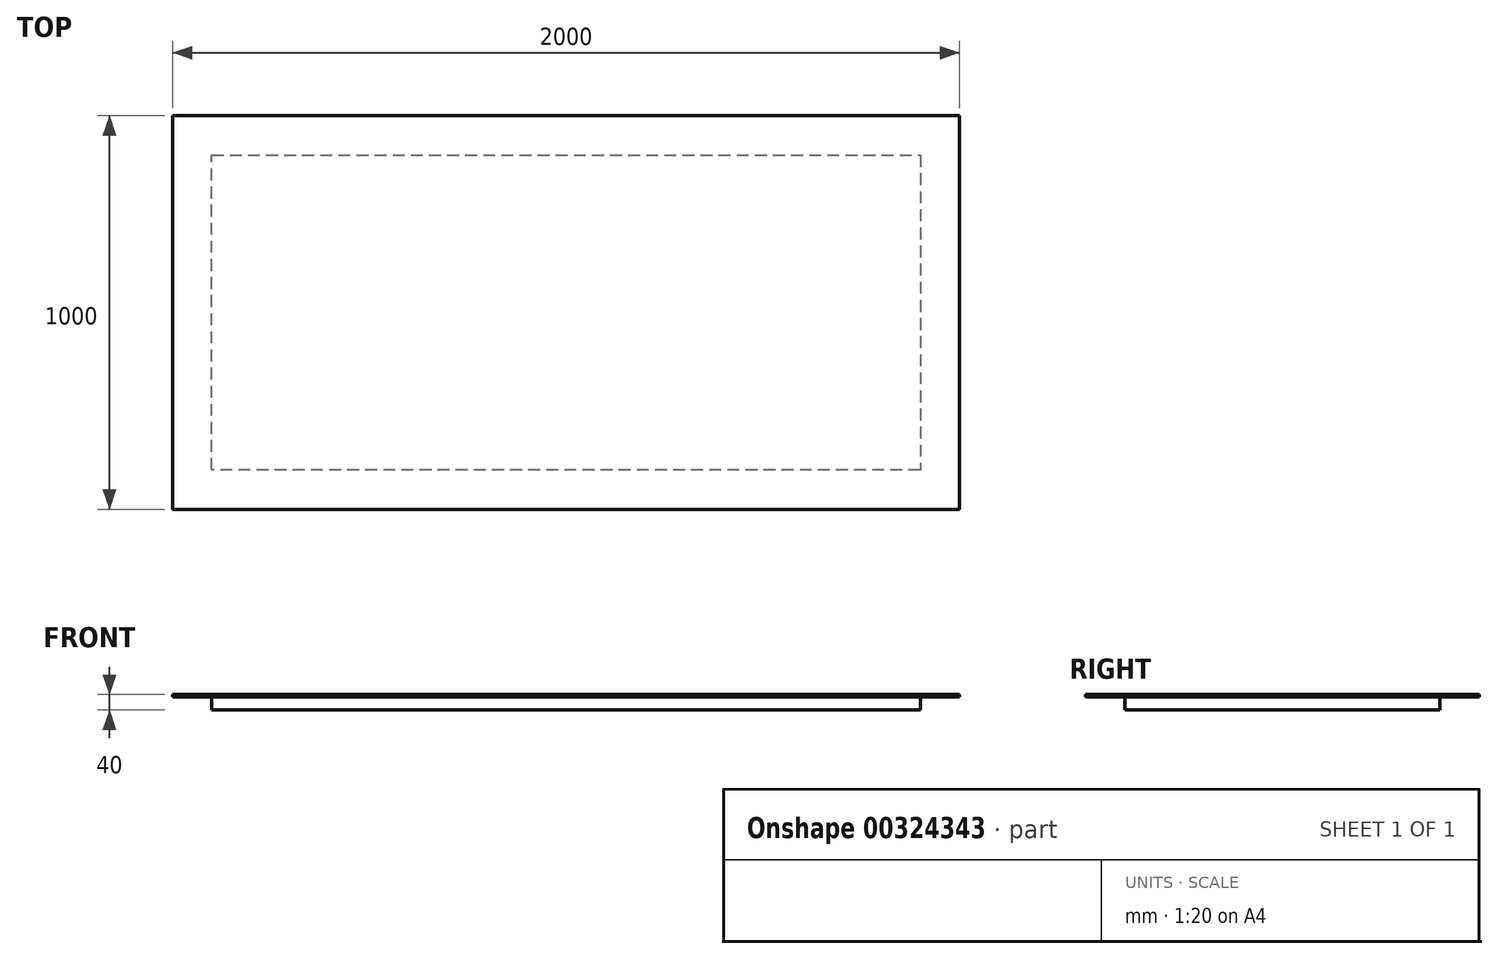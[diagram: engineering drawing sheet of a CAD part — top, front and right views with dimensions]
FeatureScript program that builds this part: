
annotation { "Feature Type Name" : "Feature", "Feature Type Description" : "" }
export const myFeature = defineFeature(function(context is Context, id is Id, definition is map)
    precondition{}
    {
        {
            var Q0;
            Q0=qCreatedBy(makeId("Top.planeOp"),FACE);
            var sketch = newSketch(context, id + "F0", { "sketchPlane" : qUnion([Q0])});
            skLineSegment(sketch, "E0.bottom", {"start": v(1000, -500) * mm, "end": v(-1000, -500) * mm});
            skLineSegment(sketch, "E0.top", {"start": v(1000, 500) * mm, "end": v(-1000, 500) * mm});
            skLineSegment(sketch, "E0.left", {"start": v(1000, -500) * mm, "end": v(1000, 500) * mm});
            skLineSegment(sketch, "E0.right", {"start": v(-1000, -500) * mm, "end": v(-1000, 500) * mm});
            skPoint(sketch, "E0.middle", {"position": v(0, 0) * mm});
            skSolve(sketch);
        }
        {
            var Q0;
            Q0=makeQuery(id+"F0.imprint","IMPRINT",FACE,{"disambiguationData":[TD([[makeQuery(id+"F0.imprint","IMPRINT",EDGE,{"derivedFrom":sQuery(id+"F0.wireOp",EDGE,"E0.bottom")}),-1.0]])]});
            extrude(context, id + "F1", {"entities" : qUnion([Q0]), "depth" : 6 * mm});
        }
        {
            var Q0;
            Q0=makeQuery(id+"F1.opExtrude","CAP_FACE",FACE,{"disambiguationData":[OSD([sQuery(id+"F0.wireOp",EDGE,"E0.bottom"),sQuery(id+"F0.wireOp",EDGE,"E0.top"),sQuery(id+"F0.wireOp",EDGE,"E0.left"),sQuery(id+"F0.wireOp",EDGE,"E0.right")])],"isStart":true});
            var sketch = newSketch(context, id + "F2", { "sketchPlane" : qUnion([Q0])});
            skLineSegment(sketch, "E1.0", {"start": v(900, -400) * mm, "end": v(900, 400) * mm});
            skLineSegment(sketch, "E1.1", {"start": v(-900, -400) * mm, "end": v(900, -400) * mm});
            skLineSegment(sketch, "E1.2", {"start": v(-900, 400) * mm, "end": v(-900, -400) * mm});
            skLineSegment(sketch, "E1.3", {"start": v(900, 400) * mm, "end": v(-900, 400) * mm});
            skLineSegment(sketch, "E2.0", {"start": v(995, -495) * mm, "end": v(995, 495) * mm});
            skLineSegment(sketch, "E2.1", {"start": v(-995, -495) * mm, "end": v(995, -495) * mm});
            skLineSegment(sketch, "E2.2", {"start": v(-995, 495) * mm, "end": v(-995, -495) * mm});
            skLineSegment(sketch, "E2.3", {"start": v(995, 495) * mm, "end": v(-995, 495) * mm});
            skSolve(sketch);
        }
        {
            var Q0;
            Q0=makeQuery(id+"F2.imprint","IMPRINT",FACE,{"disambiguationData":[TD([[makeQuery(id+"F2.imprint","IMPRINT",EDGE,{"derivedFrom":sQuery(id+"F2.wireOp",EDGE,"E1.0")}),1.0]])]});
            extrude(context, id + "F3", {"entities" : qUnion([Q0]), "operationType" : NewBodyOperationType.ADD, "depth" : 34 * mm});
        }
    });
